# Revit family: Window_Shade-Draper_Inc.-Crank_Shade
name_source: partatom
category: Specialty Equipment
units: mm (PartAtom-declared; Revit-internal decimal feet)

## family parameters
Always vertical = Yes
Classification Number = 23.30.20.11
Cut with Voids When Loaded = No
Enable Cutting in Views = No
Maintain Annotation Orientation = No
Part Type = Normal
Room Calculation Point = No
Round Connector Dimension = Use Diameter
Shared = No
Work Plane-Based = No

## types (6) — shared parameters
Case Material = Paint - Draper - White
D1 = 5/8"
Default Elevation = 0"
Description = Crank Shade
Head Box = No
Manufacturer = Draper Inc.
Model = Crank Operated FlexShade
Notes = Maximum size 120” W. x 144” H. Other sizes available. Contact Draper for details.
Product Documentation Link = http://www.draperinc.com
Product Name = Crank Operated FlexShade
Product Page URL = http://www.draperinc.com
Shade Material = Fabric - Draper - Green Screen Revive 5%
URL = http://www.DraperInc.com

## per-type parameters (varying)
| type | A1 | B1 | C Height | C Length | C1 | Depth | E1 | Endcaps Only | Length | Overall Height | Square Fascia | Width |
| Square Fascia - Large | 4 11/16" | 4 11/16" | 5' - 9 1/2" | 8' - 2 7/8" | 1 9/16" | 4 11/16" | 3/32" | No | 8' - 2 7/8" | 5' - 9 1/2" | Yes | 4 11/16" |
| Square Fascia - Small | 3 15/16" | 3 7/16" | 5' - 0" | 4' - 0" | 1 3/16" | 3 15/16" | 1/16" | No | 4' - 0" | 5' - 0" | Yes | 3 7/16" |
| HeadBox - Large | 4 11/16" | 4 11/16" | 5' - 9 1/2" | 8' - 2 7/8" | 1 9/16" | 4 11/16" | 3/32" | No | 8' - 2 7/8" | 5' - 9 1/2" | No | 4 11/16" |
| Headbox - Small | 3 15/16" | 3 7/16" | 6' - 0" | 4' - 0" | 1 3/16" | 3 15/16" | 1/16" | No | 4' - 0" | 6' - 0" | No | 3 7/16" |
| Endcaps Only - Large | 4 11/16" | 4 11/16" | 5' - 9 1/2" | 8' - 2 7/8" | 1 9/16" | 4 11/16" | 3/32" | Yes | 8' - 2 7/8" | 5' - 9 1/2" | No | 4 11/16" |
| Endcaps Only - Small | 3 15/16" | 3 7/16" | 6' - 0" | 4' - 0" | 1 3/16" | 3 15/16" | 1/16" | Yes | 4' - 0" | 6' - 0" | No | 3 7/16" |

## geometry (parser evidence)
native form markers: Blend x4, Sweep x10
no freeform markers — native parametric forms only
